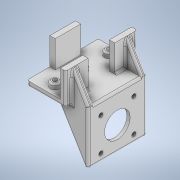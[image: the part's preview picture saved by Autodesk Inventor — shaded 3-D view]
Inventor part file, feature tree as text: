
AUTODESK INVENTOR PART (.ipt)
format: ipt  version: 2020 (Build 240168000, 168)  size: 417,280 bytes
history: native  units: in
note: dims shown in document units (in); Inventor stores cm internally (conversion verified against a paired STEP export)
features: extrude x10, sketch x10, fillet x2, chamfer x1
ambient origin geometry x8: Origin, YZ Plane, XZ Plane, XY Plane, X Axis, Y Axis, Z Axis, Center Point
bodies: Solid1 (feature_tree)
feature tree (23):
  extrude  "Extrusion1"  Depth=2.6378in
  extrude  "Extrusion2"  Depth=0.1969in
  extrude  "Extrusion6"  Depth=0.1969in
  extrude  "Extrusion8"  Depth=1.0in TaperAngle=0.0deg
  chamfer  "Chamfer1"  Distance=1.0in
  extrude  "Extrusion9"  Depth=0.3406in
  extrude  "Extrusion10"  Depth=0.1969in TaperAngle=0.0deg
  extrude  "Extrusion11"  Depth=0.0787in
  extrude  "Extrusion12"  Depth=0.0787in
  extrude  "Extrusion13"  Depth=0.0787in TaperAngle=0.0deg
  extrude  "Extrusion14"  Depth=0.0787in
  fillet  "Fillet4"  Radius=0.2362in
  fillet  "Fillet5"  Radius=0.2362in
  sketch  "Sketch1"  dims[d0=1.4331in d1=2.6378in]
  sketch  "Sketch2"  dims[d2=0.1969in d3=0.0in d4=0.1969in]
  sketch  "Sketch6"  dims[d5=0.8268in d6=0.1969in]
  sketch  "Sketch8"  dims[d7=0.8268in d8=1.0in d9=0.0in]
  sketch  "Sketch9"  dims[d26=0.1969in]
  sketch  "Sketch10"  dims[d27=0.9449in d28=1.0in d29=0.0in]
  sketch  "Sketch11"  dims[d37=0.3406in d38=0.3406in]
  sketch  "Sketch12"  dims[d39=0.3406in d40=0.1969in d41=0.0in]
  sketch  "Sketch13"  dims[d42=0.0591in d43=0.0787in d44=45.0deg d45=0.1575in]
  sketch  "Sketch14"  dims[d46=0.1575in d47=0.1575in d48=0.7874in d49=0.0in d50=0.2362in d51=0.2362in d52=0.2362in d53=0.0984in d54=0.0in d55=2.1654in d56=0.1969in d57=0.1969in d58=0.5906in d59=0.0in d60=0.1969in d61=0.1969in d62=0.1181in d63=1.7717in d64=0.0in d65=2.7559in d66=0.0in d67=0.9449in d68=0.1575in d69=0.1575in d70=0.1575in d71=0.1575in d72=2.7559in d73=0.0in d74=0.0787in d75=0.0787in d10=0.0197in d11=0.0344in d13=0.0197in d14=0.0344in d15=0.0197in d16=0.0344in]
